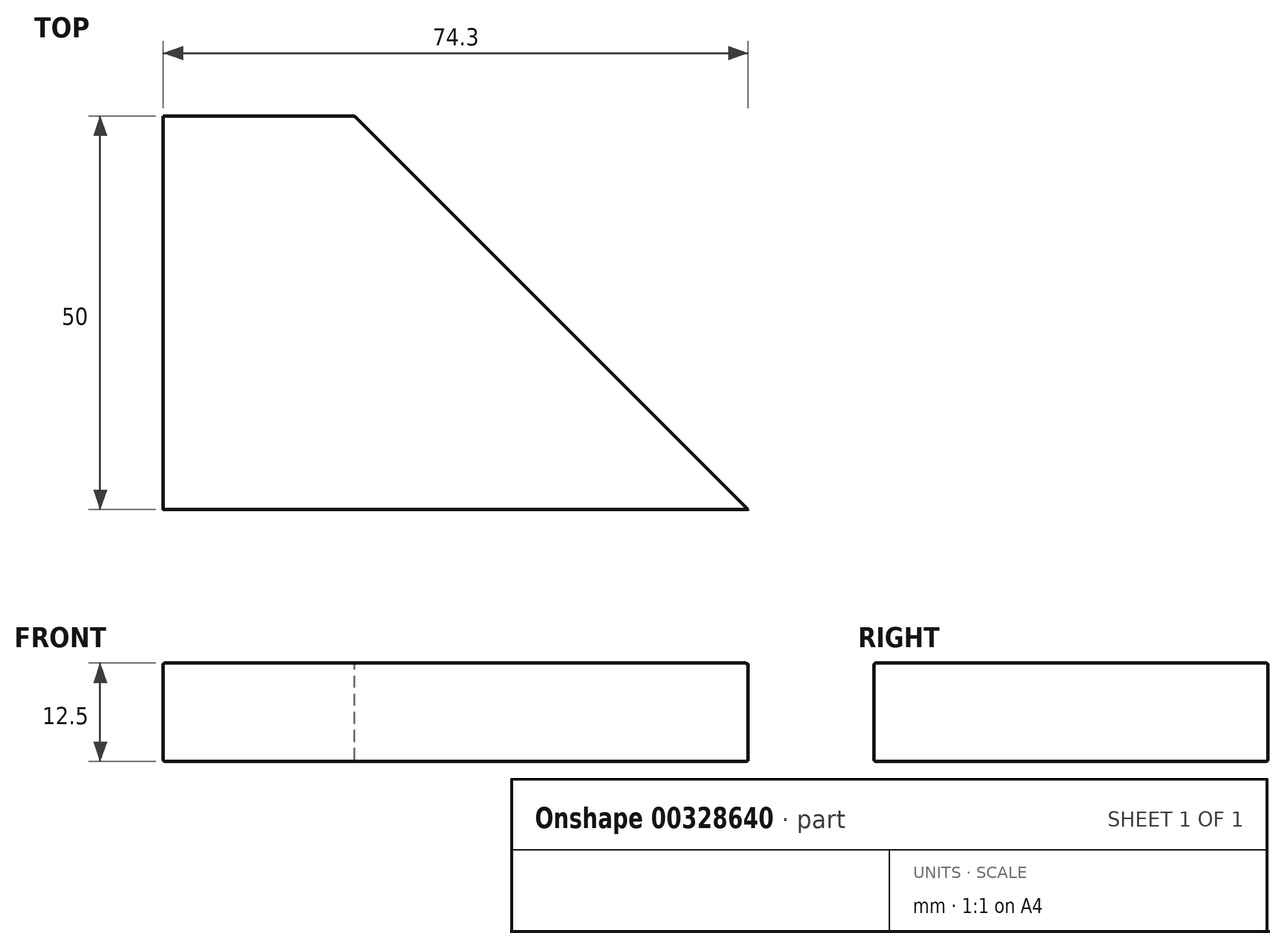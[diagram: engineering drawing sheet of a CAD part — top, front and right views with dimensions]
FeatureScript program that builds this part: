
annotation { "Feature Type Name" : "Feature", "Feature Type Description" : "" }
export const myFeature = defineFeature(function(context is Context, id is Id, definition is map)
    precondition{}
    {
        {
            var Q0;
            Q0=qCreatedBy(makeId("Top.planeOp"),FACE);
            var sketch = newSketch(context, id + "F0", { "sketchPlane" : qUnion([Q0])});
            skLineSegment(sketch, "E0.bottom", {"start": v(0, 0) * mm, "end": v(74.3, 0) * mm});
            skLineSegment(sketch, "E0.top", {"start": v(0, 50) * mm, "end": v(24.3, 50) * mm});
            skLineSegment(sketch, "E0.left", {"start": v(0, 0) * mm, "end": v(0, 50) * mm});
            skLineSegment(sketch, "E1", {"start": v(74.3, 0) * mm, "end": v(24.3, 50) * mm});
            skPoint(sketch, "E2.orphan", {"position": v(48.6, 50) * mm});
            skSolve(sketch);
        }
        {
            var Q0;
            Q0=qSketchRegion(id+"F0",true);
            extrude(context, id + "F1", {"entities" : qUnion([Q0]), "oppositeDirection" : true, "depth" : 12.5 * mm});
        }
        {
            var Q0;
            Q0=makeQuery(id+"F1.opExtrude","CAP_FACE",FACE,{"disambiguationData":[OSD([sQuery(id+"F0.wireOp",EDGE,"E0.bottom"),sQuery(id+"F0.wireOp",EDGE,"E0.top"),sQuery(id+"F0.wireOp",EDGE,"E0.left"),sQuery(id+"F0.wireOp",EDGE,"E0.right")])],"isStart":true});
            var Q1;
            Q1=makeQuery(id+"F1.opExtrude","CAP_FACE",FACE,{"disambiguationData":[OSD([sQuery(id+"F0.wireOp",EDGE,"E0.bottom"),sQuery(id+"F0.wireOp",EDGE,"E0.top"),sQuery(id+"F0.wireOp",EDGE,"E0.left"),sQuery(id+"F0.wireOp",EDGE,"E0.right")])],"isStart":false});
            fillet(context, id + "F2", {"entities" : qUnion([Q0, Q1]), "radius" : .2 * mm, "tangentPropagation" : true, "allowEdgeOverflow" : false});
        }
    });
